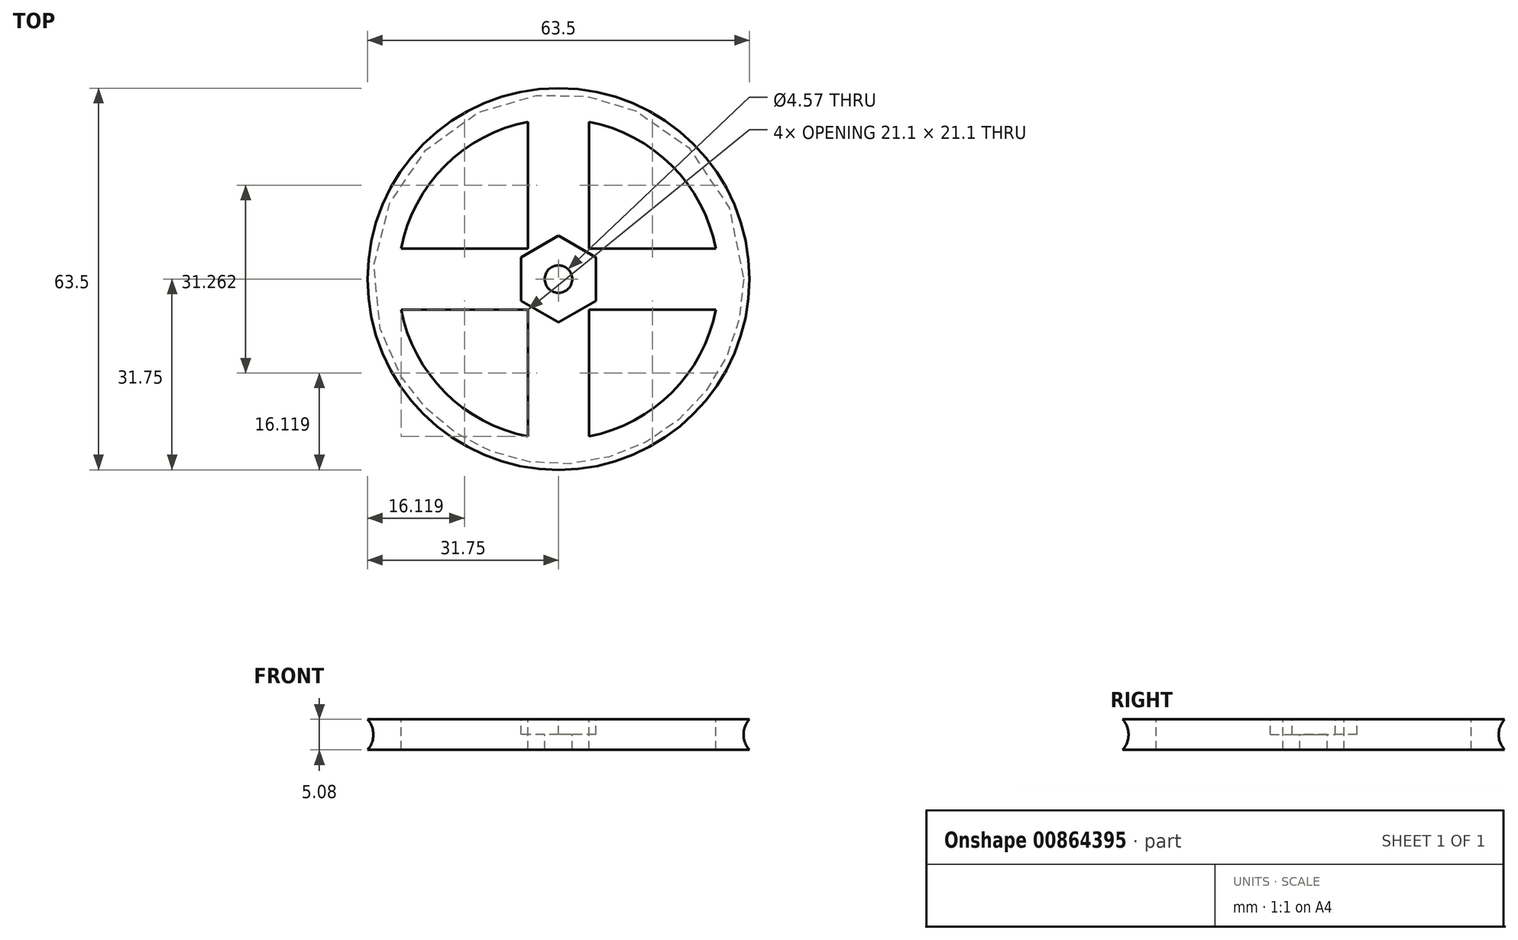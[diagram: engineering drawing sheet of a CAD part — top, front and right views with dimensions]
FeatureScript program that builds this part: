
annotation { "Feature Type Name" : "Feature", "Feature Type Description" : "" }
export const myFeature = defineFeature(function(context is Context, id is Id, definition is map)
    precondition{}
    {
        {
            var Q0;
            Q0=qCreatedBy(makeId("Front.planeOp"),FACE);
            var sketch = newSketch(context, id + "F0", { "sketchPlane" : qUnion([Q0])});
            skLineSegment(sketch, "E0", {"start": v(-31.75, 5.08) * mm, "end": v(0, 5.08) * mm});
            skLineSegment(sketch, "E1", {"start": v(0, 5.08) * mm, "end": v(0, 0) * mm});
            skLineSegment(sketch, "E2", {"start": v(0, 0) * mm, "end": v(-31.75, 0) * mm});
            skArc(sketch, "E3", {"start": v(-31.75, 0) * mm, "mid": v(-30.78, 2.54) * mm, "end": v(-31.75, 5.08) * mm});
            skSolve(sketch);
        }
        {
            var Q0;
            Q0=makeQuery(id+"F0.imprint","IMPRINT",FACE,{"disambiguationData":[TD([[makeQuery(id+"F0.imprint","IMPRINT",EDGE,{"derivedFrom":sQuery(id+"F0.wireOp",EDGE,"E0")}),-1.0]])]});
            var Q1;
            Q1=sQuery(id+"F0.wireOp",EDGE,"E1");
            revolve(context, id + "F1", {"surfaceOperationType" : NewSurfaceOperationType.NEW, "entities" : qUnion([Q0]), "axis" : qUnion([Q1]), "revolveType" : RevolveType.FULL});
        }
        {
            var Q0;
            Q0=makeQuery(id+"F1.opRevolve","SWEPT_FACE",FACE,{"disambiguationData":[OSD([sQuery(id+"F0.wireOp",EDGE,"E0")])]});
            var sketch = newSketch(context, id + "F2", { "sketchPlane" : qUnion([Q0])});
            skArc(sketch, "E4", {"start": v(-31.75, 0) * mm, "mid": v(-22.45, -22.45) * mm, "end": v(0, -31.75) * mm, "construction": true});
            skLineSegment(sketch, "E5", {"start": v(0, -31.75) * mm, "end": v(0, 0) * mm, "construction": true});
            skLineSegment(sketch, "E6", {"start": v(-31.75, 0) * mm, "end": v(0, 0) * mm, "construction": true});
            skArc(sketch, "E7.0", {"start": v(-26.18, -5.08) * mm, "mid": v(-18.86, -18.86) * mm, "end": v(-5.08, -26.18) * mm});
            skLineSegment(sketch, "E7.1", {"start": v(-26.18, -5.08) * mm, "end": v(-5.08, -5.08) * mm});
            skLineSegment(sketch, "E7.2", {"start": v(-5.08, -26.18) * mm, "end": v(-5.08, -5.08) * mm});
            skLineSegment(sketch, "E8.MirrorCS", {"start": v(-26.18, 5.08) * mm, "end": v(-5.08, 5.08) * mm});
            skLineSegment(sketch, "E9.MirrorCS", {"start": v(-5.08, 26.18) * mm, "end": v(-5.08, 5.08) * mm});
            skArc(sketch, "E10.MirrorCS", {"start": v(-26.18, 5.08) * mm, "mid": v(-18.86, 18.86) * mm, "end": v(-5.08, 26.18) * mm});
            skLineSegment(sketch, "E11.MirrorCS", {"start": v(5.08, -26.18) * mm, "end": v(5.08, -5.08) * mm});
            skLineSegment(sketch, "E12.MirrorCS", {"start": v(26.18, -5.08) * mm, "end": v(5.08, -5.08) * mm});
            skArc(sketch, "E13.MirrorCS", {"start": v(26.18, -5.08) * mm, "mid": v(18.86, -18.86) * mm, "end": v(5.08, -26.18) * mm});
            skLineSegment(sketch, "E14.MirrorCS", {"start": v(26.18, 5.08) * mm, "end": v(5.08, 5.08) * mm});
            skLineSegment(sketch, "E15.MirrorCS", {"start": v(5.08, 26.18) * mm, "end": v(5.08, 5.08) * mm});
            skArc(sketch, "E16.MirrorCS", {"start": v(26.18, 5.08) * mm, "mid": v(18.86, 18.86) * mm, "end": v(5.08, 26.18) * mm});
            skSolve(sketch);
        }
        {
            var Q0;
            Q0 = qSketchRegion(id + "F2", true);
            extrude(context, id + "F3", {"entities" : qUnion([Q0]), "operationType" : NewBodyOperationType.REMOVE, "endBound" : BoundingType.THROUGH_ALL, "oppositeDirection" : true, "depth" : 25.4 * mm, "offsetDistance" : 25.4 * mm});
        }
        {
            var Q0;
            Q0=makeQuery(id+"F1.opRevolve","SWEPT_FACE",FACE,{"disambiguationData":[OSD([sQuery(id+"F0.wireOp",EDGE,"E0")])]});
            var sketch = newSketch(context, id + "F4", { "sketchPlane" : qUnion([Q0])});
            skLineSegment(sketch, "E17", {"start": v(-6.24, -3.6) * mm, "end": v(-6.24, 3.6) * mm});
            skLineSegment(sketch, "E18", {"start": v(-6.24, 3.6) * mm, "end": v(0, 7.2) * mm});
            skLineSegment(sketch, "E19", {"start": v(0, 7.2) * mm, "end": v(6.24, 3.6) * mm});
            skLineSegment(sketch, "E20", {"start": v(6.24, 3.6) * mm, "end": v(6.24, -3.6) * mm});
            skLineSegment(sketch, "E21", {"start": v(6.24, -3.6) * mm, "end": v(0, -7.2) * mm});
            skLineSegment(sketch, "E22", {"start": v(0, -7.2) * mm, "end": v(-6.24, -3.6) * mm});
            skSolve(sketch);
        }
        {
            var Q0;
            Q0 = qSketchRegion(id + "F4", true);
            extrude(context, id + "F5", {"entities" : qUnion([Q0]), "operationType" : NewBodyOperationType.REMOVE, "oppositeDirection" : true, "depth" : 2.54 * mm, "offsetDistance" : 25.4 * mm});
        }
        {
            var Q0;
            Q0=makeQuery(id+"F5.boolean.opBoolean","COPY",FACE,{"derivedFrom":makeQuery(id+"F5.opExtrude","CAP_FACE",FACE,{"disambiguationData":[OSD([sQuery(id+"F4.wireOp",EDGE,"E17"),sQuery(id+"F4.wireOp",EDGE,"E18"),sQuery(id+"F4.wireOp",EDGE,"E19"),sQuery(id+"F4.wireOp",EDGE,"E20"),sQuery(id+"F4.wireOp",EDGE,"E21"),sQuery(id+"F4.wireOp",EDGE,"E22")])],"isStart":false})});
            var sketch = newSketch(context, id + "F6", { "sketchPlane" : qUnion([Q0])});
            skCircle(sketch, "E23", {"center": v(0, 0) * mm, "radius": 2.29 * mm});
            skSolve(sketch);
        }
        {
            var Q0;
            Q0 = qSketchRegion(id + "F6", true);
            extrude(context, id + "F7", {"entities" : qUnion([Q0]), "operationType" : NewBodyOperationType.REMOVE, "endBound" : BoundingType.THROUGH_ALL, "oppositeDirection" : true, "depth" : 25.4 * mm, "offsetDistance" : 25.4 * mm});
        }
    });
